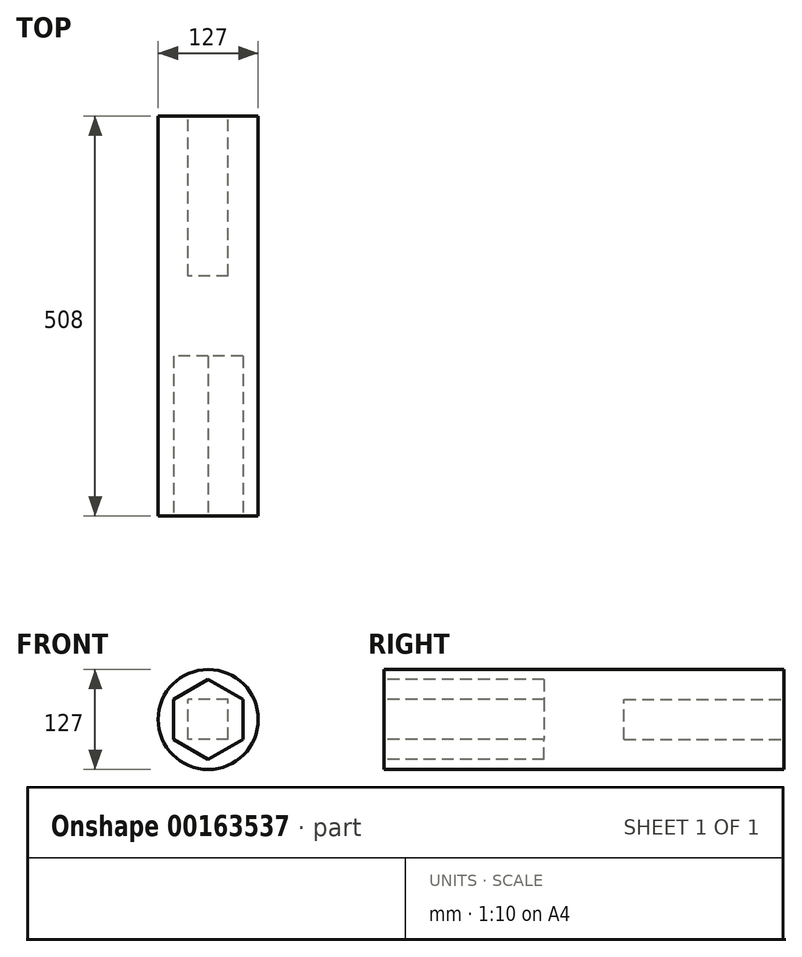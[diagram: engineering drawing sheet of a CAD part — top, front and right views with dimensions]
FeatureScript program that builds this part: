
annotation { "Feature Type Name" : "Feature", "Feature Type Description" : "" }
export const myFeature = defineFeature(function(context is Context, id is Id, definition is map)
    precondition{}
    {
        {
            var Q0;
            Q0=qCreatedBy(makeId("Front.planeOp"),FACE);
            var sketch = newSketch(context, id + "F0", { "sketchPlane" : qUnion([Q0])});
            skCircle(sketch, "E0", {"center": v(0, 0) * mm, "radius": 63.5 * mm});
            skSolve(sketch);
        }
        {
            var Q0;
            Q0=makeQuery(id+"F0.imprint","IMPRINT",FACE,{"disambiguationData":[TD([[makeQuery(id+"F0.imprint","IMPRINT",EDGE,{"derivedFrom":sQuery(id+"F0.wireOp",EDGE,"E0")}),1.0]])]});
            extrude(context, id + "F1", {"entities" : qUnion([Q0]), "endBound" : BoundingType.SYMMETRIC, "depth" : 508 * mm});
        }
        {
            var Q0;
            Q0=makeQuery(id+"F1.opExtrude","CAP_FACE",FACE,{"disambiguationData":[OSD([sQuery(id+"F0.wireOp",EDGE,"E0")])],"isStart":true});
            var sketch = newSketch(context, id + "F2", { "sketchPlane" : qUnion([Q0])});
            skLineSegment(sketch, "E1.bottom", {"start": v(-25.4, -25.4) * mm, "end": v(25.4, -25.4) * mm});
            skLineSegment(sketch, "E1.top", {"start": v(-25.4, 25.4) * mm, "end": v(25.4, 25.4) * mm});
            skLineSegment(sketch, "E1.left", {"start": v(-25.4, -25.4) * mm, "end": v(-25.4, 25.4) * mm});
            skLineSegment(sketch, "E1.right", {"start": v(25.4, -25.4) * mm, "end": v(25.4, 25.4) * mm});
            skPoint(sketch, "E1.middle", {"position": v(0, 0) * mm});
            skSolve(sketch);
        }
        {
            var Q0;
            Q0=makeQuery(id+"F2.imprint","IMPRINT",FACE,{"disambiguationData":[TD([[makeQuery(id+"F2.imprint","IMPRINT",EDGE,{"derivedFrom":sQuery(id+"F2.wireOp",EDGE,"E1.bottom")}),1.0]])]});
            extrude(context, id + "F3", {"entities" : qUnion([Q0]), "operationType" : NewBodyOperationType.REMOVE, "oppositeDirection" : true, "depth" : 203.2 * mm});
        }
        {
            var Q0;
            Q0=makeQuery(id+"F1.opExtrude","CAP_FACE",FACE,{"disambiguationData":[OSD([sQuery(id+"F0.wireOp",EDGE,"E0")])],"isStart":false});
            var sketch = newSketch(context, id + "F4", { "sketchPlane" : qUnion([Q0])});
            skCircle(sketch, "E2.cCircle", {"center": v(0, 0) * mm, "radius": 50.8 * mm, "construction": true});
            skLineSegment(sketch, "E2.0", {"start": v(0, -50.8) * mm, "end": v(-44, -25.4) * mm});
            skLineSegment(sketch, "E2.1", {"start": v(-44, -25.4) * mm, "end": v(-44, 25.4) * mm});
            skLineSegment(sketch, "E2.2", {"start": v(-44, 25.4) * mm, "end": v(0, 50.8) * mm});
            skLineSegment(sketch, "E2.3", {"start": v(0, 50.8) * mm, "end": v(44, 25.4) * mm});
            skLineSegment(sketch, "E2.4", {"start": v(44, 25.4) * mm, "end": v(44, -25.4) * mm});
            skLineSegment(sketch, "E2.5", {"start": v(44, -25.4) * mm, "end": v(0, -50.8) * mm});
            skSolve(sketch);
        }
        {
            var Q0;
            Q0=makeQuery(id+"F4.imprint","IMPRINT",FACE,{"disambiguationData":[TD([[makeQuery(id+"F4.imprint","IMPRINT",EDGE,{"derivedFrom":sQuery(id+"F4.wireOp",EDGE,"E2.0")}),-1.0]])]});
            extrude(context, id + "F5", {"entities" : qUnion([Q0]), "operationType" : NewBodyOperationType.REMOVE, "oppositeDirection" : true, "depth" : 203.2 * mm});
        }
    });
